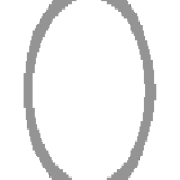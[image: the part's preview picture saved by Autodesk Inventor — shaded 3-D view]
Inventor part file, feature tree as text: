
AUTODESK INVENTOR PART (.ipt)
format: ipt  version: 2021 (Build 250183000, 183)  size: 140,800 bytes
history: native  units: in
note: dims shown in document units (in); Inventor stores cm internally (conversion verified against a paired STEP export)
features: other x5, sketch x2, sweep x1, plane x1
ambient origin geometry x8: Origin, YZ Plane, XZ Plane, XY Plane, X Axis, Y Axis, Z Axis, Center Point
bodies: Solid1 (feature_tree), Body (feature_tree)
feature tree (9):
  other  "Driven Length"
  other  "Frame Generator"
  other  "Start Plane"
  other  "End Plane"
  sweep  "Sweep Path"
  other  "Orientation Work Plane"
  sketch  "Sketch2"  dims[d0=1.0in d1=0.065in]
  plane  "Work Plane3"
  sketch  "Sketch3"  dims[d2=1.1738in d4=-0.0in d5=1.1738in d8=90.0deg d9=1.1738in d10=0.0in d11=0.0in]
